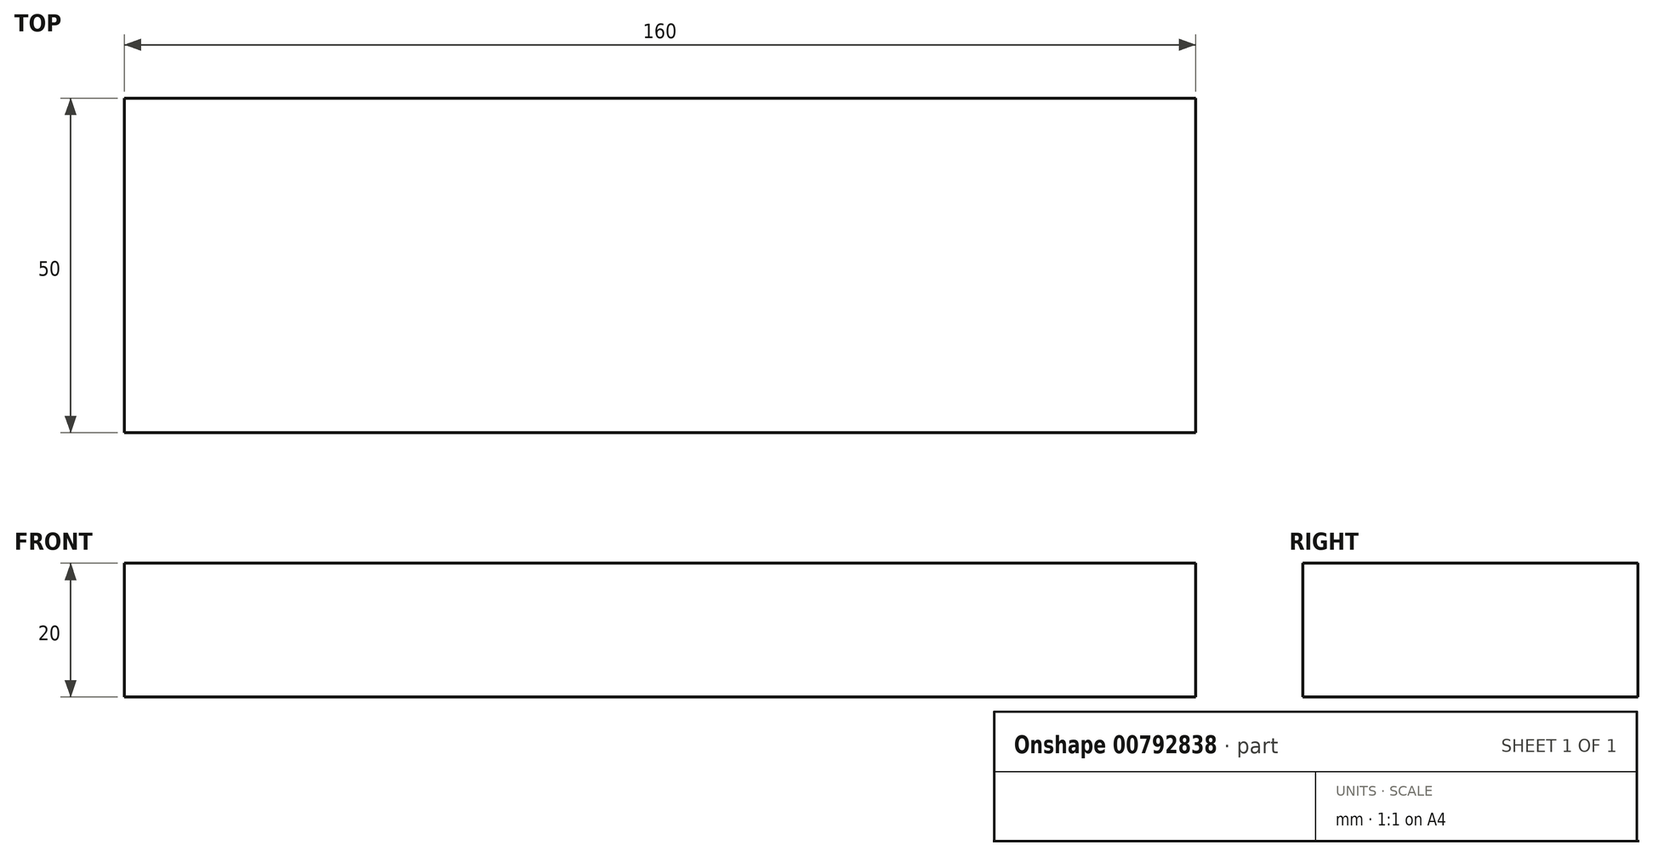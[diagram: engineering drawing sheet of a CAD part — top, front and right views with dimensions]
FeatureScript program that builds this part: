
annotation { "Feature Type Name" : "Feature", "Feature Type Description" : "" }
export const myFeature = defineFeature(function(context is Context, id is Id, definition is map)
    precondition{}
    {
        {
            var Q0;
            Q0=qCreatedBy(makeId("Front.planeOp"),FACE);
            var sketch = newSketch(context, id + "F0", { "sketchPlane" : qUnion([Q0])});
            skLineSegment(sketch, "E0", {"start": v(0, 277.68) * mm, "end": v(0, -283.93) * mm, "construction": true});
            skLineSegment(sketch, "E1", {"start": v(0, -41.64) * mm, "end": v(-170, -41.64) * mm});
            skLineSegment(sketch, "E2", {"start": v(-170, -41.64) * mm, "end": v(-170, -169.64) * mm});
            skLineSegment(sketch, "E3", {"start": v(-170, -169.64) * mm, "end": v(-150, -169.64) * mm});
            skLineSegment(sketch, "E4", {"start": v(-150, -169.64) * mm, "end": v(-150, -61.64) * mm});
            skLineSegment(sketch, "E5", {"start": v(-150, -61.64) * mm, "end": v(0, -61.64) * mm});
            skLineSegment(sketch, "E6.MirrorCS", {"start": v(150, -61.64) * mm, "end": v(0, -61.64) * mm});
            skLineSegment(sketch, "E7.MirrorCS", {"start": v(0, -41.64) * mm, "end": v(170, -41.64) * mm});
            skLineSegment(sketch, "E8.MirrorCS", {"start": v(170, -41.64) * mm, "end": v(170, -169.64) * mm});
            skLineSegment(sketch, "E9.MirrorCS", {"start": v(150, -169.64) * mm, "end": v(150, -61.64) * mm});
            skLineSegment(sketch, "E10.MirrorCS", {"start": v(170, -169.64) * mm, "end": v(150, -169.64) * mm});
            skLineSegment(sketch, "E11", {"start": v(-30, -61.64) * mm, "end": v(-30, -169.64) * mm});
            skLineSegment(sketch, "E12", {"start": v(-30, -169.64) * mm, "end": v(0, -169.64) * mm});
            skLineSegment(sketch, "E13.MirrorCS", {"start": v(30, -169.64) * mm, "end": v(0, -169.64) * mm});
            skLineSegment(sketch, "E14.MirrorCS", {"start": v(30, -61.64) * mm, "end": v(30, -169.64) * mm});
            skSolve(sketch);
        }
        {
            var Q0;
            Q0 = qSketchRegion(id + "F0", true);
            extrude(context, id + "F1", {"entities" : qUnion([Q0]), "depth" : 50 * mm, "offsetDistance" : 25 * mm});
        }
        {
            var Q0;
            Q0=makeQuery(id+"F1.opExtrude","CAP_FACE",FACE,{"disambiguationData":[OSD([sQuery(id+"F0.wireOp",EDGE,"E1"),sQuery(id+"F0.wireOp",EDGE,"E2"),sQuery(id+"F0.wireOp",EDGE,"E3"),sQuery(id+"F0.wireOp",EDGE,"E4"),sQuery(id+"F0.wireOp",EDGE,"E5"),sQuery(id+"F0.wireOp",EDGE,"E6.MirrorCS"),sQuery(id+"F0.wireOp",EDGE,"E7.MirrorCS"),sQuery(id+"F0.wireOp",EDGE,"E8.MirrorCS"),sQuery(id+"F0.wireOp",EDGE,"E9.MirrorCS"),sQuery(id+"F0.wireOp",EDGE,"E10.MirrorCS"),sQuery(id+"F0.wireOp",EDGE,"E11"),sQuery(id+"F0.wireOp",EDGE,"E12"),sQuery(id+"F0.wireOp",EDGE,"E13.MirrorCS"),sQuery(id+"F0.wireOp",EDGE,"E14.MirrorCS")])],"isStart":false});
            var sketch = newSketch(context, id + "F2", { "sketchPlane" : qUnion([Q0])});
            skLineSegment(sketch, "E15", {"start": v(-180.5, -41.64) * mm, "end": v(191.1, -41.64) * mm});
            skLineSegment(sketch, "E16", {"start": v(191.1, -61.64) * mm, "end": v(-180.5, -61.64) * mm});
            skLineSegment(sketch, "E17", {"start": v(-180.5, -61.64) * mm, "end": v(-180.5, -41.64) * mm});
            skLineSegment(sketch, "E18", {"start": v(45.13, -61.64) * mm, "end": v(45.13, -186.28) * mm});
            skLineSegment(sketch, "E19", {"start": v(45.13, -186.28) * mm, "end": v(191.1, -186.28) * mm});
            skLineSegment(sketch, "E20", {"start": v(191.1, -186.28) * mm, "end": v(191.1, -61.64) * mm});
            skLineSegment(sketch, "E21", {"start": v(-180.5, -61.64) * mm, "end": v(-180.5, -186.28) * mm});
            skLineSegment(sketch, "E22", {"start": v(-180.5, -186.28) * mm, "end": v(-133.02, -186.28) * mm});
            skLineSegment(sketch, "E23", {"start": v(-133.02, -186.28) * mm, "end": v(-133.02, -61.64) * mm});
            skLineSegment(sketch, "E24", {"start": v(10, -41.64) * mm, "end": v(10, -61.64) * mm});
            skLineSegment(sketch, "E25", {"start": v(-133.02, -186.28) * mm, "end": v(45.13, -186.28) * mm});
            skSolve(sketch);
        }
        {
            var Q0;
            Q0 = qSketchRegion(id + "F2", true);
            extrude(context, id + "F3", {"entities" : qUnion([Q0]), "operationType" : NewBodyOperationType.REMOVE, "oppositeDirection" : true, "depth" : 50 * mm, "offsetDistance" : 25 * mm});
        }
    });
